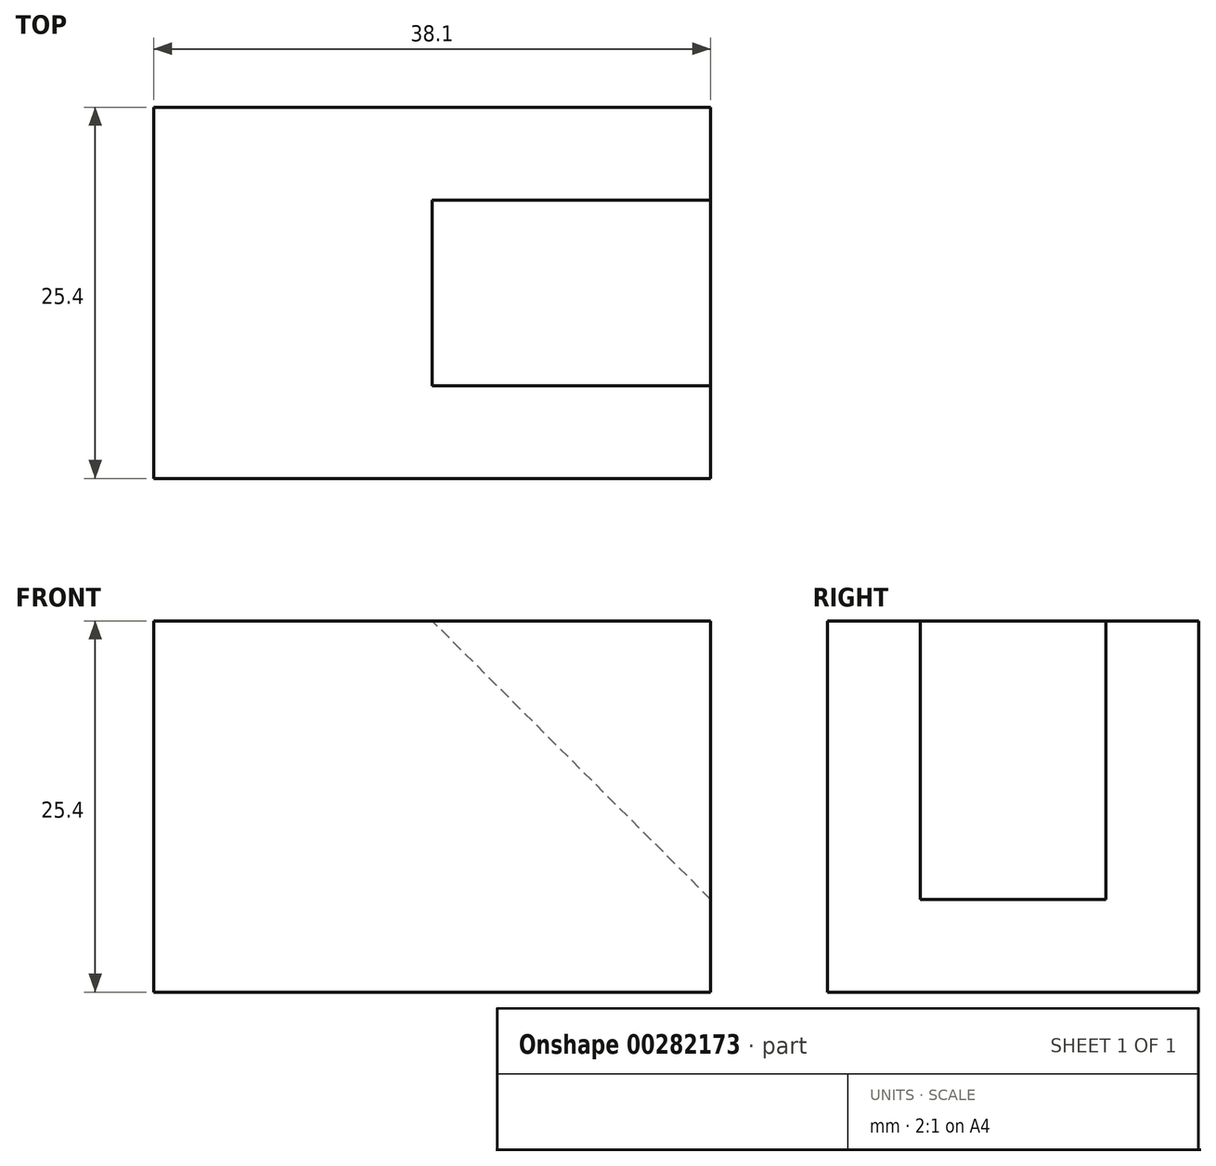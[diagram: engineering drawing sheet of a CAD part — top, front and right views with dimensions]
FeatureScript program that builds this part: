
annotation { "Feature Type Name" : "Feature", "Feature Type Description" : "" }
export const myFeature = defineFeature(function(context is Context, id is Id, definition is map)
    precondition{}
    {
        {
            var Q0;
            Q0=qCreatedBy(makeId("Top.planeOp"),FACE);
            var sketch = newSketch(context, id + "F0", { "sketchPlane" : qUnion([Q0])});
            skLineSegment(sketch, "E0", {"start": v(0, 0) * mm, "end": v(0, 25.4) * mm});
            skLineSegment(sketch, "E1", {"start": v(0, 25.4) * mm, "end": v(38.1, 25.4) * mm});
            skLineSegment(sketch, "E2", {"start": v(38.1, 25.4) * mm, "end": v(38.1, 0) * mm});
            skLineSegment(sketch, "E3", {"start": v(38.1, 0) * mm, "end": v(0, 0) * mm});
            skSolve(sketch);
        }
        {
            var Q0;
            Q0=makeQuery(id+"F0.imprint","IMPRINT",FACE,{"disambiguationData":[TD([[makeQuery(id+"F0.imprint","IMPRINT",EDGE,{"derivedFrom":sQuery(id+"F0.wireOp",EDGE,"E0")}),-1.0]])]});
            extrude(context, id + "F1", {"entities" : qUnion([Q0]), "depth" : 25.4 * mm});
        }
        {
            var Q0;
            Q0=makeQuery(id+"F1.opExtrude","SWEPT_FACE",FACE,{"disambiguationData":[OSD([sQuery(id+"F0.wireOp",EDGE,"E3")])]});
            var sketch = newSketch(context, id + "F2", { "sketchPlane" : qUnion([Q0])});
            skLineSegment(sketch, "E4", {"start": v(19.05, 25.4) * mm, "end": v(38.1, 25.4) * mm});
            skLineSegment(sketch, "E5", {"start": v(38.1, 25.4) * mm, "end": v(38.1, 6.35) * mm});
            skLineSegment(sketch, "E6", {"start": v(38.1, 6.35) * mm, "end": v(19.05, 25.4) * mm});
            skSolve(sketch);
        }
        {
            var Q0;
            Q0=makeQuery(id+"F2.imprint","IMPRINT",FACE,{"disambiguationData":[TD([[makeQuery(id+"F2.imprint","IMPRINT",EDGE,{"derivedFrom":sQuery(id+"F2.wireOp",EDGE,"E4")}),1.0]])]});
            extrude(context, id + "F3", {"entities" : qUnion([Q0]), "operationType" : NewBodyOperationType.REMOVE, "oppositeDirection" : true, "depth" : 19.05 * mm, "hasSecondDirection" : true, "secondDirectionOppositeDirection" : true, "secondDirectionDepth" : 6.35 * mm});
        }
    });
